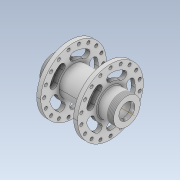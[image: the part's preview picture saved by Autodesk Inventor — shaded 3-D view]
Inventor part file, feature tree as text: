
AUTODESK INVENTOR PART (.ipt)
format: ipt  version: 2021 (Build 250183000, 183)  size: 451,584 bytes
history: native  units: mm
features: other x5, sketch x4, thread x3, revolve x2, extrude x2, fillet x2, pattern_circular x1, mirror x1
ambient origin geometry x8: Origin, YZ Plane, XZ Plane, XY Plane, X Axis, Y Axis, Z Axis, Center Point
bodies: Body1 (feature_tree), Body2 (feature_tree)
feature tree (20):
  other  "LlantaUser Library-Bike Weell.ipt"
  revolve  "Revolución1"  [1 undecoded]
  revolve  "Revolución3"  [1 undecoded]
  pattern_circular  "Patrón circular2"  Angle=90.0deg  [1 undecoded]
  mirror  "Simetría1"
  extrude  "Extrusión1"  Depth=60.0mm TaperAngle=360.0deg
  thread  "Rosca3"  [1 undecoded]
  thread  "Rosca4"  [1 undecoded]
  fillet  "Empalme2"  Radius=10.0mm
  extrude  "Extrusión2"  Depth=12.0mm TaperAngle=0.0deg
  fillet  "Empalme3"  Radius=1.5mm
  thread  "Rosca5"  [1 undecoded]
  other  "Solid1::LlantaUser Library-Bike Weell.ipt"
  other  "OperaciónIdentificador1"
  sketch  "Boceto1"  dims[d0=10.0mm d1=5.0mm]
  sketch  "Boceto3"  dims[d2=5.0mm d3=3.0mm]
  other  "Sólido3"
  sketch  "Boceto4"  dims[d4=90.0deg]
  sketch  "Boceto5"  dims[d5=4.0mm d10=90.0deg d11=60.0mm d12=360.0deg d19=1.5mm d20=8.0mm d21=0.0mm d22=10.0mm d23=0.0mm d24=12.0mm d25=0.0mm d26=1.0mm d27=1.5mm d28=8.0mm d29=0.0mm d30=1.0mm d31=8.0mm d32=0.0mm]
  other  "Sólido1"
note: 6 required parameter values undecoded (feature->parameter linkage not recoverable at this tier; creation-order binding heuristic only, values carry confidence <= 0.55)